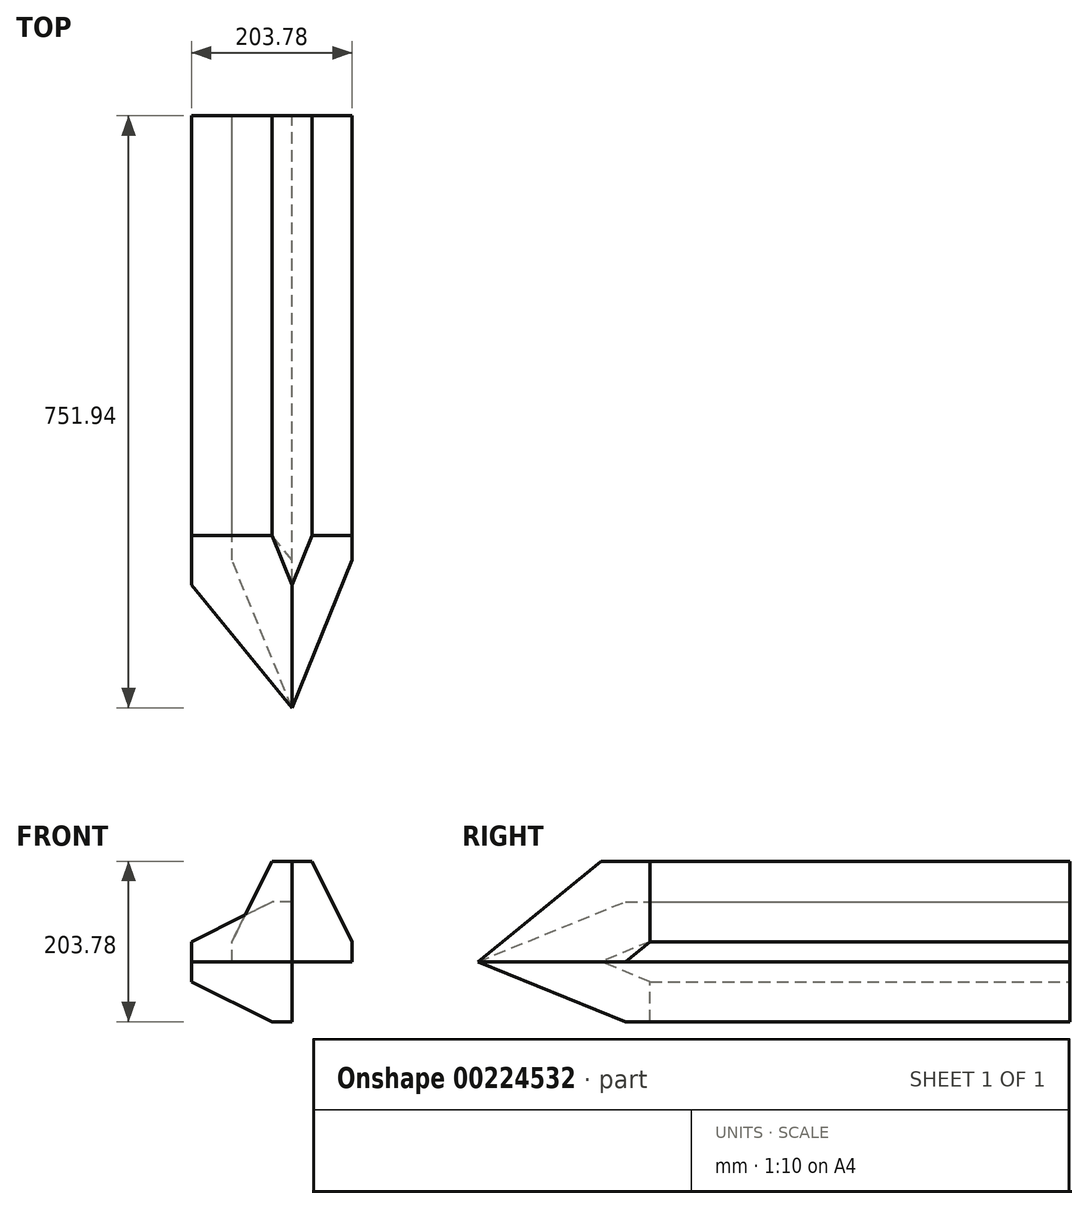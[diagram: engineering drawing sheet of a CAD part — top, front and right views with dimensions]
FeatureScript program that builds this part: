
annotation { "Feature Type Name" : "Feature", "Feature Type Description" : "" }
export const myFeature = defineFeature(function(context is Context, id is Id, definition is map)
    precondition{}
    {
        {
            var Q0;
            Q0=qCreatedBy(makeId("Front.planeOp"),FACE);
            var sketch = newSketch(context, id + "F0", { "sketchPlane" : qUnion([Q0])});
            skLineSegment(sketch, "E0", {"start": v(0, 76.2) * mm, "end": v(-25.4, 76.2) * mm});
            skLineSegment(sketch, "E1.MirrorCS", {"start": v(0, -76.2) * mm, "end": v(-25.4, -76.2) * mm});
            skLineSegment(sketch, "E2", {"start": v(-127.58, 0) * mm, "end": v(-127.58, 25.4) * mm});
            skLineSegment(sketch, "E3", {"start": v(-127.58, 25.4) * mm, "end": v(-25.4, 76.2) * mm});
            skLineSegment(sketch, "E4.MirrorCS", {"start": v(127.58, 25.4) * mm, "end": v(25.4, 76.2) * mm});
            skLineSegment(sketch, "E5.MirrorCS", {"start": v(127.58, 0) * mm, "end": v(127.58, 25.4) * mm});
            skLineSegment(sketch, "E6.MirrorCS", {"start": v(0, 76.2) * mm, "end": v(25.4, 76.2) * mm});
            skLineSegment(sketch, "E7.MirrorCS", {"start": v(0, -76.2) * mm, "end": v(25.4, -76.2) * mm});
            skLineSegment(sketch, "E8.MirrorCS", {"start": v(127.58, -25.4) * mm, "end": v(25.4, -76.2) * mm});
            skLineSegment(sketch, "E9.MirrorCS", {"start": v(-127.58, -25.4) * mm, "end": v(-25.4, -76.2) * mm});
            skLineSegment(sketch, "E10.MirrorCS", {"start": v(-127.58, 0) * mm, "end": v(-127.58, -25.4) * mm});
            skLineSegment(sketch, "E11.MirrorCS", {"start": v(127.58, 0) * mm, "end": v(127.58, -25.4) * mm});
            skLineSegment(sketch, "E12", {"start": v(0, 76.2) * mm, "end": v(0, -76.2) * mm});
            skSolve(sketch);
        }
        {
            var Q0;
            Q0=makeQuery(id+"F0.imprint","IMPRINT",FACE,{"disambiguationData":[TD([[makeQuery(id+"F0.imprint","IMPRINT",EDGE,{"derivedFrom":sQuery(id+"F0.wireOp",EDGE,"E0")}),1.0]])]});
            extrude(context, id + "F1", {"entities" : qUnion([Q0]), "depth" : 762 * mm});
        }
        {
            var Q0;
            Q0=makeQuery(id+"F1.opExtrude","CAP_EDGE",EDGE,{"disambiguationData":[OSD([sQuery(id+"F0.wireOp",EDGE,"E3")])],"isStart":false});
            var Q1;
            Q1=makeQuery(id+"F1.opExtrude","CAP_EDGE",EDGE,{"disambiguationData":[OSD([sQuery(id+"F0.wireOp",EDGE,"E4.MirrorCS")])],"isStart":false});
            var Q2;
            Q2=makeQuery(id+"F1.opExtrude","CAP_EDGE",EDGE,{"disambiguationData":[OSD([sQuery(id+"F0.wireOp",EDGE,"E8.MirrorCS")])],"isStart":false});
            var Q3;
            Q3=makeQuery(id+"F1.opExtrude","CAP_EDGE",EDGE,{"disambiguationData":[OSD([sQuery(id+"F0.wireOp",EDGE,"E9.MirrorCS")])],"isStart":false});
            chamfer(context, id + "F2", {"entities" : qUnion([Q0, Q1, Q2, Q3]), "chamferType" : ChamferType.OFFSET_ANGLE, "width" : 228.6 * mm, "oppositeDirection" : false, "angle" : 20 * degree, "tangentPropagation" : true});
        }
        {
            var Q0;
            Q0=makeQuery(id+"F1.opExtrude","SWEPT_FACE",FACE,{"disambiguationData":[OSD([sQuery(id+"F0.wireOp",EDGE,"E12")])]});
            var sketch = newSketch(context, id + "F3", { "sketchPlane" : qUnion([Q0])});
            skLineSegment(sketch, "E13", {"start": v(-751.94, 0) * mm, "end": v(-501.94, 0) * mm});
            skLineSegment(sketch, "E14", {"start": v(0, 0) * mm, "end": v(-200, 0) * mm});
            skSolve(sketch);
        }
        {
            var Q0;
            Q0=makeQuery(id+"F1.opExtrude","SWEPT_BODY",BODY,{"disambiguationData":[OSD([sQuery(id+"F0.wireOp",EDGE,"E0"),sQuery(id+"F0.wireOp",EDGE,"E2"),sQuery(id+"F0.wireOp",EDGE,"E3"),sQuery(id+"F0.wireOp",EDGE,"E1.MirrorCS"),sQuery(id+"F0.wireOp",EDGE,"E9.MirrorCS"),sQuery(id+"F0.wireOp",EDGE,"E10.MirrorCS"),sQuery(id+"F0.wireOp",EDGE,"E12")])]});
            var Q1;
            Q1=sQuery(id+"F3.wireOp",EDGE,"E13");
            transform(context, id + "F4", {"entities" : qUnion([Q0]), "transformType" : TransformType.ROTATION, "transformAxis" : qUnion([Q1]), "angle" : 90 * degree, "makeCopy" : true});
        }
    });
